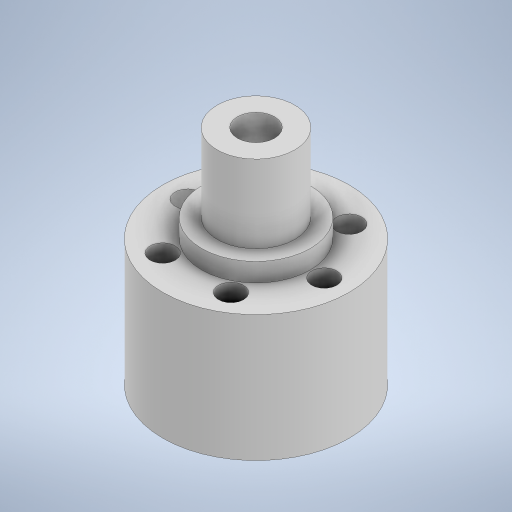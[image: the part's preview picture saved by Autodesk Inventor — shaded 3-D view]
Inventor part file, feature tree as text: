
AUTODESK INVENTOR PART (.ipt)
format: ipt  version: 2024 (Build 280153000, 153)  size: 281,600 bytes
history: native  units: mm
features: extrude x5, sketch x5, projected_geometry x1
ambient origin geometry x8: Origin, YZ Plane, XZ Plane, XY Plane, X Axis, Y Axis, Z Axis, Center Point
bodies: Solid1 (feature_tree)
feature tree (11):
  extrude  "Extrusion1"  Depth=6.0mm TaperAngle=0.0deg
  extrude  "Extrusion2"  Depth=25.0mm TaperAngle=0.0deg
  extrude  "Extrusion3"  Depth=60.0mm
  extrude  "Extrusion4"  Depth=12.0mm
  extrude  "Extrusion5"  Depth=22.0mm
  sketch  "Sketch1"  dims[d0=35.0mm d1=6.0mm d2=0.0mm]
  sketch  "Sketch2"  dims[d3=25.0mm d4=25.0mm d5=0.0mm]
  sketch  "Sketch3"  dims[d6=100.0mm d7=0.0mm d8=60.0mm]
  sketch  "Sketch4"  dims[d9=24.0mm d10=0.0mm d11=12.0mm]
  sketch  "Sketch5"  dims[d12=22.0mm d13=8.1mm d14=60.0mm d16=360.0deg d18=16.7mm d19=0.0mm]
  projected_geometry  "Projected Loop1"
